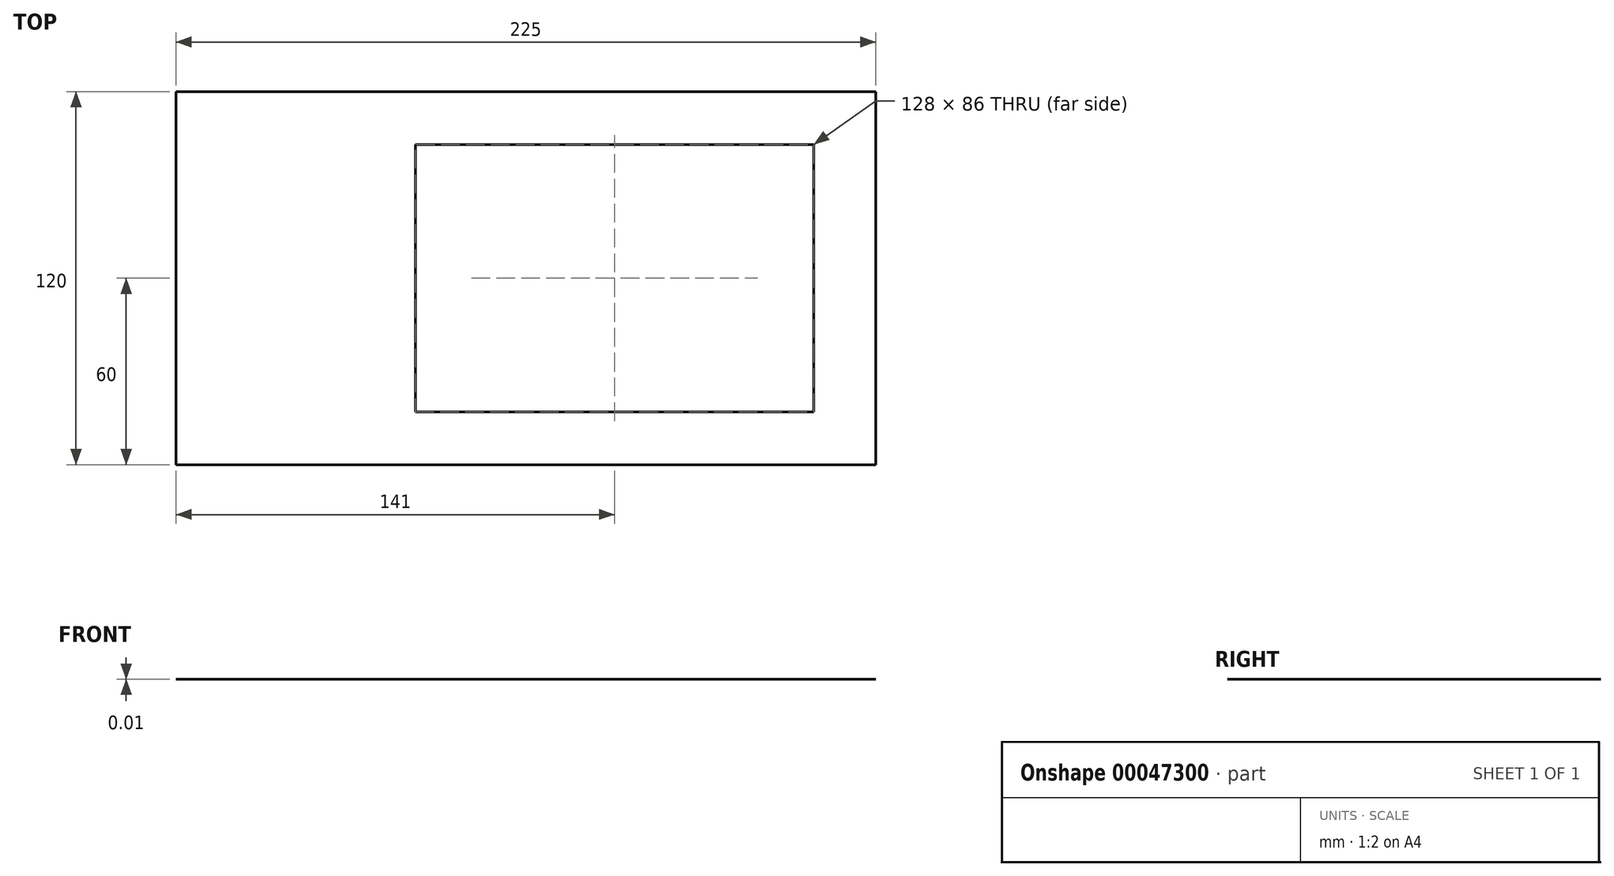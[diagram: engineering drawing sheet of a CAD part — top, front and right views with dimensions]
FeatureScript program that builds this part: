
annotation { "Feature Type Name" : "Feature", "Feature Type Description" : "" }
export const myFeature = defineFeature(function(context is Context, id is Id, definition is map)
    precondition{}
    {
        {
            var Q0;
            Q0=qCreatedBy(makeId("Top.planeOp"),FACE);
            var sketch = newSketch(context, id + "F0", { "sketchPlane" : qUnion([Q0])});
            skLineSegment(sketch, "E0.rect.bottom", {"start": v(112.5, -60) * mm, "end": v(-112.5, -60) * mm});
            skLineSegment(sketch, "E0.rect.top", {"start": v(112.5, 60) * mm, "end": v(-112.5, 60) * mm});
            skLineSegment(sketch, "E0.rect.left", {"start": v(112.5, -60) * mm, "end": v(112.5, 60) * mm});
            skLineSegment(sketch, "E0.rect.right", {"start": v(-112.5, -60) * mm, "end": v(-112.5, 60) * mm});
            skPoint(sketch, "E0.rect.middle", {"position": v(0, 0) * mm});
            skSolve(sketch);
        }
        {
            var Q0;
            Q0=makeQuery(id+"F0.imprint","IMPRINT",FACE,{"disambiguationData":[TD([[makeQuery(id+"F0.imprint","IMPRINT",EDGE,{"derivedFrom":sQuery(id+"F0.wireOp",EDGE,"E0.rect.bottom")}),-1.0]])]});
            extrude(context, id + "F1", {"entities" : qUnion([Q0]), "depth" : 1 / 101.6 * mm});
        }
        {
            var Q0;
            Q0=makeQuery(id+"F1.opExtrude","CAP_FACE",FACE,{"disambiguationData":[OSD([sQuery(id+"F0.wireOp",EDGE,"E0.rect.bottom"),sQuery(id+"F0.wireOp",EDGE,"E0.rect.top"),sQuery(id+"F0.wireOp",EDGE,"E0.rect.left"),sQuery(id+"F0.wireOp",EDGE,"E0.rect.right")])],"isStart":false});
            var sketch = newSketch(context, id + "F2", { "sketchPlane" : qUnion([Q0])});
            skLineSegment(sketch, "E1.bottom", {"start": v(-35.5, 43) * mm, "end": v(92.5, 43) * mm});
            skLineSegment(sketch, "E1.top", {"start": v(-35.5, -43) * mm, "end": v(92.5, -43) * mm});
            skLineSegment(sketch, "E1.left", {"start": v(-35.5, 43) * mm, "end": v(-35.5, -43) * mm});
            skLineSegment(sketch, "E1.right", {"start": v(92.5, 43) * mm, "end": v(92.5, -43) * mm});
            skLineSegment(sketch, "E2", {"start": v(92.5, 0) * mm, "end": v(112.5, 0) * mm, "construction": true});
            skLineSegment(sketch, "E3", {"start": v(28.5, -43) * mm, "end": v(28.5, -60) * mm, "construction": true});
            skLineSegment(sketch, "E4", {"start": v(28.5, 43) * mm, "end": v(28.5, 60) * mm, "construction": true});
            skSolve(sketch);
        }
        {
            var Q0;
            Q0=qSketchRegion(id+"F2",true);
            extrude(context, id + "F3", {"entities" : qUnion([Q0]), "operationType" : NewBodyOperationType.REMOVE, "oppositeDirection" : true, "depth" : 4.8 * mm});
        }
    });
